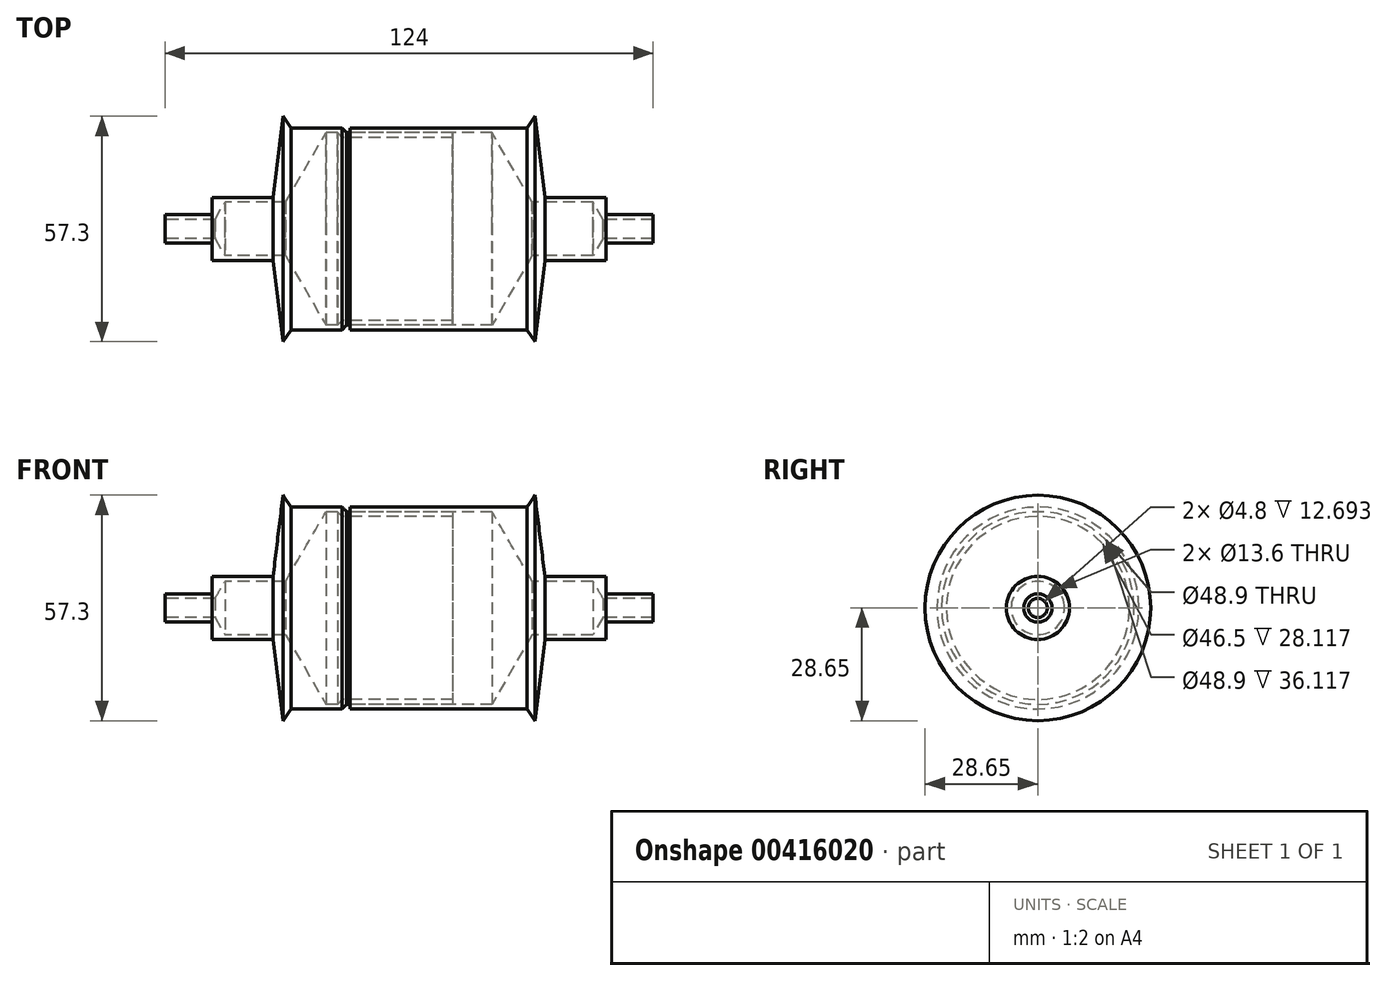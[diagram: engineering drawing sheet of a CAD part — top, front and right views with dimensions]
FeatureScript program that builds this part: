
annotation { "Feature Type Name" : "Feature", "Feature Type Description" : "" }
export const myFeature = defineFeature(function(context is Context, id is Id, definition is map)
    precondition{}
    {
        {
            var Q0;
            Q0=qCreatedBy(makeId("Front.planeOp"),FACE);
            var sketch = newSketch(context, id + "F0", { "sketchPlane" : qUnion([Q0])});
            skLineSegment(sketch, "E0", {"start": v(62, 3.6) * mm, "end": v(50, 3.6) * mm});
            skLineSegment(sketch, "E1", {"start": v(50, 8) * mm, "end": v(32, 8) * mm});
            skLineSegment(sketch, "E2", {"start": v(32, 28.65) * mm, "end": v(30, 25.65) * mm});
            skLineSegment(sketch, "E3", {"start": v(30, 25.65) * mm, "end": v(-15, 25.65) * mm});
            skLineSegment(sketch, "E4", {"start": v(-15, 25.65) * mm, "end": v(-15, 24.45) * mm});
            skLineSegment(sketch, "E5", {"start": v(-15, 24.45) * mm, "end": v(21.12, 24.45) * mm});
            skLineSegment(sketch, "E6", {"start": v(49.3, 2.4) * mm, "end": v(62, 2.4) * mm});
            skLineSegment(sketch, "E7", {"start": v(31.3, 6.8) * mm, "end": v(21.12, 24.45) * mm});
            skLineSegment(sketch, "E8", {"start": v(0, 0) * mm, "end": v(74.87, 0) * mm, "construction": true});
            skLineSegment(sketch, "E9", {"start": v(50, 8) * mm, "end": v(50, 3.6) * mm});
            skLineSegment(sketch, "E10", {"start": v(62, 3.6) * mm, "end": v(62, 2.4) * mm});
            skLineSegment(sketch, "E11", {"start": v(32, 8) * mm, "end": v(30.96, 7.4) * mm, "construction": true});
            skLineSegment(sketch, "E12", {"start": v(32, 8) * mm, "end": v(32, 28.65) * mm, "construction": true});
            skLineSegment(sketch, "E13", {"start": v(46.77, 6.8) * mm, "end": v(31.3, 6.8) * mm});
            skLineSegment(sketch, "E14", {"start": v(49.3, 2.4) * mm, "end": v(46.77, 6.8) * mm});
            skLineSegment(sketch, "E15", {"start": v(46.77, 6.8) * mm, "end": v(46.77, 8) * mm, "construction": true});
            skLineSegment(sketch, "E16", {"start": v(50, 3.6) * mm, "end": v(48.96, 3) * mm, "construction": true});
            skLineSegment(sketch, "E17.MirrorCS", {"start": v(-32, 28.65) * mm, "end": v(-30, 25.65) * mm, "construction": true});
            skLineSegment(sketch, "E18", {"start": v(32, 28.65) * mm, "end": v(34.54, 8) * mm});
            skSolve(sketch);
        }
        {
            var Q0;
            Q0=makeQuery(id+"F0.imprint","IMPRINT",FACE,{"disambiguationData":[TD([[makeQuery(id+"F0.imprint","IMPRINT",EDGE,{"derivedFrom":sQuery(id+"F0.wireOp",EDGE,"E0")}),1.0]])]});
            var Q1;
            Q1=sQuery(id+"F0.wireOp",EDGE,"E8");
            var Q2;
            Q2=sQuery(id+"F0.wireOp",EDGE,"E0");
            var Q3;
            Q3=sQuery(id+"F0.wireOp",EDGE,"asEibcgI-jTcl-GQX3-IyWU-w3ePdzjDX9v1");
            var Q4;
            Q4=sQuery(id+"F0.wireOp",EDGE,"E1");
            var Q5;
            Q5=sQuery(id+"F0.wireOp",EDGE,"39413bb7-427a-4a06-9a64-f9cf2ffad437.0");
            var Q6;
            Q6=sQuery(id+"F0.wireOp",EDGE,"E2");
            var Q7;
            Q7=sQuery(id+"F0.wireOp",EDGE,"E3");
            var Q8;
            Q8=sQuery(id+"F0.wireOp",EDGE,"E4");
            var Q9;
            Q9=sQuery(id+"F0.wireOp",EDGE,"E5");
            var Q10;
            Q10=sQuery(id+"F0.wireOp",EDGE,"E7");
            var Q11;
            Q11=sQuery(id+"F0.wireOp",EDGE,"E6");
            var Q12;
            Q12=sQuery(id+"F0.wireOp",EDGE,"b334028a-bd6f-4eda-a3a3-d9cde917d21f.0");
            var Q13;
            Q13=sQuery(id+"F0.wireOp",EDGE,"E8");
            revolve(context, id + "F1", {"entities" : qUnion([Q0]), "surfaceEntities" : qUnion([Q1, Q2, Q3, Q4, Q5, Q6, Q7, Q8, Q9, Q10, Q11, Q12]), "axis" : qUnion([Q13]), "revolveType" : RevolveType.FULL});
        }
        {
            var Q0;
            Q0=qCreatedBy(makeId("Front.planeOp"),FACE);
            var sketch = newSketch(context, id + "F2", { "sketchPlane" : qUnion([Q0])});
            skLineSegment(sketch, "E19.MirrorCS", {"start": v(-30, 25.65) * mm, "end": v(-17, 25.65) * mm});
            skLineSegment(sketch, "E20.MirrorCS", {"start": v(-18.2, 24.45) * mm, "end": v(-21.12, 24.45) * mm});
            skLineSegment(sketch, "E21.MirrorCS", {"start": v(-31.3, 6.8) * mm, "end": v(-21.12, 24.45) * mm});
            skLineSegment(sketch, "E22.MirrorCS", {"start": v(-30, 25.65) * mm, "end": v(-32, 28.65) * mm});
            skLineSegment(sketch, "E23.MirrorCS", {"start": v(-32, 8) * mm, "end": v(-32, 28.65) * mm, "construction": true});
            skLineSegment(sketch, "E24.MirrorCS", {"start": v(-32, 8) * mm, "end": v(-50, 8) * mm});
            skLineSegment(sketch, "E25.MirrorCS", {"start": v(-46.77, 6.8) * mm, "end": v(-31.3, 6.8) * mm});
            skLineSegment(sketch, "E26.MirrorCS", {"start": v(-46.77, 6.8) * mm, "end": v(-49.3, 2.4) * mm});
            skLineSegment(sketch, "E27.MirrorCS", {"start": v(-50, 3.6) * mm, "end": v(-50, 8) * mm});
            skLineSegment(sketch, "E28.MirrorCS", {"start": v(-50, 3.6) * mm, "end": v(-62, 3.6) * mm});
            skLineSegment(sketch, "E29.MirrorCS", {"start": v(-62, 2.4) * mm, "end": v(-49.3, 2.4) * mm});
            skLineSegment(sketch, "E30.MirrorCS", {"start": v(-62, 3.6) * mm, "end": v(-62, 2.4) * mm});
            skLineSegment(sketch, "E31", {"start": v(-50, 3.6) * mm, "end": v(-48.96, 3) * mm, "construction": true});
            skLineSegment(sketch, "E32", {"start": v(-32, 8) * mm, "end": v(-30.96, 7.4) * mm, "construction": true});
            skLineSegment(sketch, "E33", {"start": v(-46.77, 6.8) * mm, "end": v(-46.77, 8) * mm, "construction": true});
            skLineSegment(sketch, "E34", {"start": v(-17, 25.65) * mm, "end": v(-15.8, 24.45) * mm});
            skLineSegment(sketch, "E35", {"start": v(-18.2, 24.45) * mm, "end": v(-17, 23.25) * mm});
            skLineSegment(sketch, "E36", {"start": v(-15.8, 24.45) * mm, "end": v(11.12, 24.45) * mm});
            skLineSegment(sketch, "E37.MirrorCS", {"start": v(31.3, 6.8) * mm, "end": v(21.12, 24.45) * mm, "construction": true});
            skLineSegment(sketch, "E38", {"start": v(21.12, 24.45) * mm, "end": v(11.12, 24.45) * mm, "construction": true});
            skLineSegment(sketch, "E39", {"start": v(11.12, 24.45) * mm, "end": v(11.12, 23.25) * mm});
            skLineSegment(sketch, "E40", {"start": v(11.12, 23.25) * mm, "end": v(-17, 23.25) * mm});
            skLineSegment(sketch, "E41", {"start": v(-15.8, 24.45) * mm, "end": v(-17, 23.25) * mm});
            skLineSegment(sketch, "E42", {"start": v(-17, 25.65) * mm, "end": v(-18.2, 24.45) * mm});
            skLineSegment(sketch, "E43", {"start": v(-32, 28.65) * mm, "end": v(-34.54, 8) * mm});
            skSolve(sketch);
        }
        {
            var Q0;
            Q0=qSketchRegion(id+"F2",true);
            var Q1;
            Q1=sQuery(id+"F0.wireOp",EDGE,"E8");
            revolve(context, id + "F3", {"entities" : qUnion([Q0]), "axis" : qUnion([Q1]), "revolveType" : RevolveType.FULL});
        }
    });
